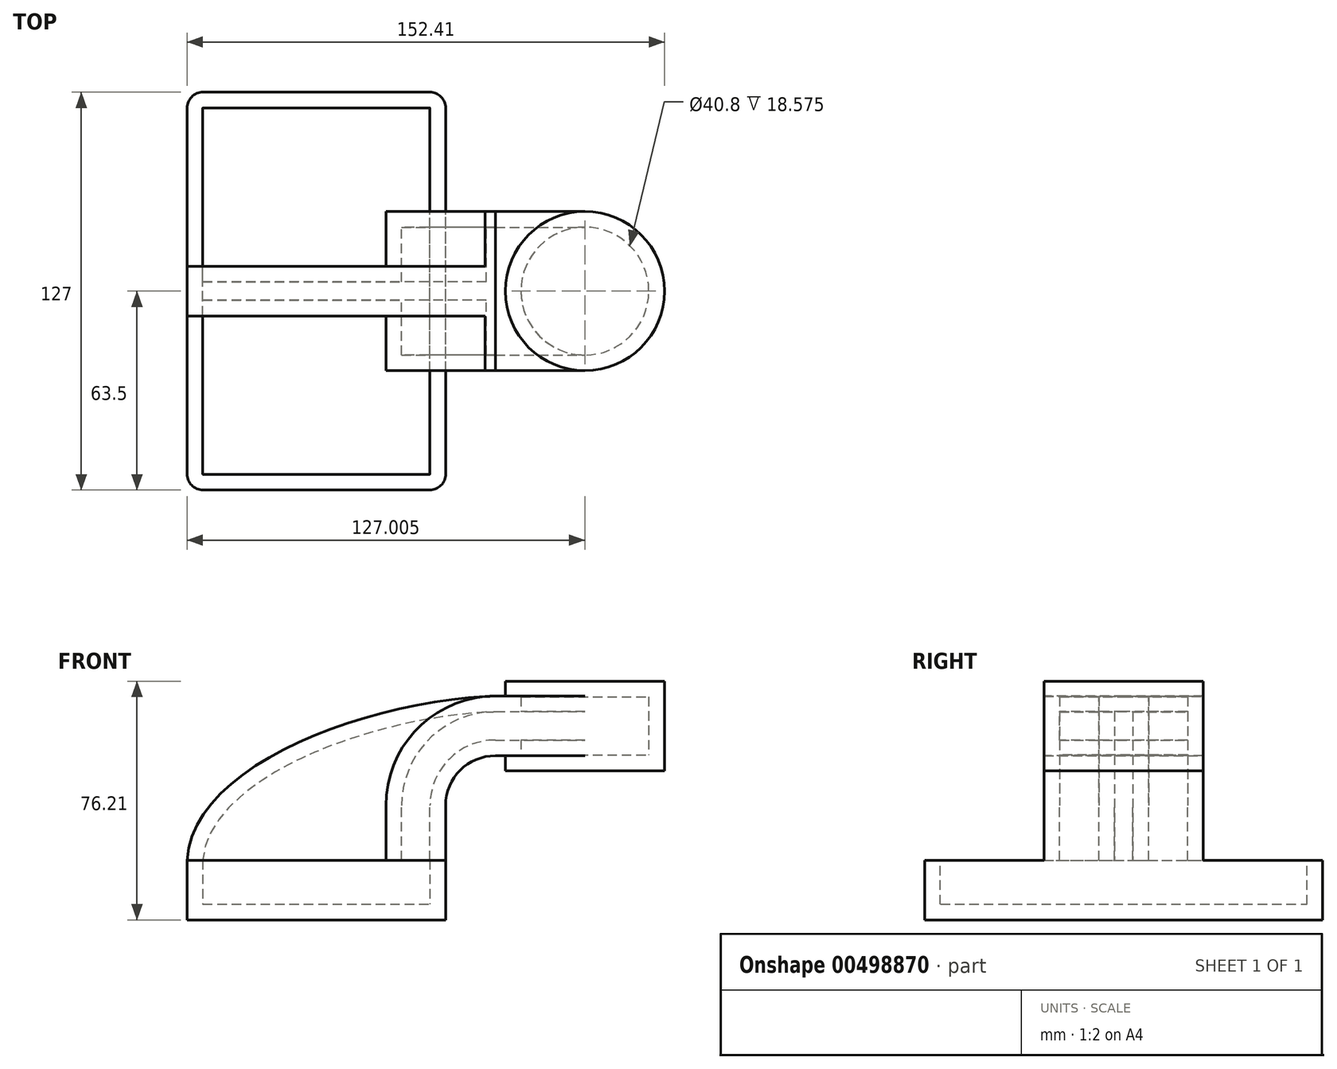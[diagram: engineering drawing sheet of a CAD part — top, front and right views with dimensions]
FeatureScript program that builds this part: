
annotation { "Feature Type Name" : "Feature", "Feature Type Description" : "" }
export const myFeature = defineFeature(function(context is Context, id is Id, definition is map)
    precondition{}
    {
        {
            var Q0;
            Q0=qCreatedBy(makeId("Front.planeOp"),FACE);
            var sketch = newSketch(context, id + "F0", { "sketchPlane" : qUnion([Q0])});
            skLineSegment(sketch, "E0.rect.bottom", {"start": v(-41.28, 9.52) * mm, "end": v(41.28, 9.52) * mm});
            skLineSegment(sketch, "E0.rect.top", {"start": v(-41.28, -9.52) * mm, "end": v(41.28, -9.52) * mm});
            skLineSegment(sketch, "E0.rect.left", {"start": v(-41.28, 9.52) * mm, "end": v(-41.28, -9.52) * mm});
            skLineSegment(sketch, "E0.rect.right", {"start": v(41.28, 9.52) * mm, "end": v(41.28, -9.52) * mm});
            skPoint(sketch, "E0.rect.middle", {"position": v(0, 0) * mm});
            skLineSegment(sketch, "E1", {"start": v(41.28, 9.52) * mm, "end": v(41.28, 27) * mm});
            skArc(sketch, "E2", {"start": v(41.28, 27) * mm, "mid": v(45.92, 38.23) * mm, "end": v(57.15, 42.88) * mm});
            skLineSegment(sketch, "E3", {"start": v(57.15, 42.88) * mm, "end": v(85.72, 42.88) * mm});
            skLineSegment(sketch, "E4.rect.bottom", {"start": v(60.32, 38.1) * mm, "end": v(111.12, 38.1) * mm});
            skLineSegment(sketch, "E4.rect.top", {"start": v(60.32, 66.68) * mm, "end": v(111.12, 66.68) * mm});
            skLineSegment(sketch, "E4.rect.left", {"start": v(60.32, 38.1) * mm, "end": v(60.32, 66.68) * mm});
            skLineSegment(sketch, "E4.rect.right", {"start": v(111.13, 38.1) * mm, "end": v(111.12, 66.68) * mm});
            skPoint(sketch, "E4.rect.middle", {"position": v(85.72, 52.39) * mm});
            skLineSegment(sketch, "E5.0", {"start": v(57.15, 61.93) * mm, "end": v(85.72, 61.93) * mm});
            skArc(sketch, "E5.1", {"start": v(22.23, 27) * mm, "mid": v(32.45, 51.7) * mm, "end": v(57.15, 61.93) * mm});
            skLineSegment(sketch, "E5.2", {"start": v(22.23, 9.52) * mm, "end": v(22.23, 27) * mm});
            skLineSegment(sketch, "E6", {"start": v(85.72, 38.1) * mm, "end": v(85.72, 66.68) * mm});
            skFitSpline(sketch, "E7", {"points": [v(-41.28, 9.53) * mm, v(57.15, 61.93) * mm], "startDerivative": vector(5.2, 92.34) * mm, "endDerivative": vector(120.92, 4.22) * mm});
            skSolve(sketch);
        }
        {
            var Q0;
            Q0=makeQuery(id+"F0.imprint","IMPRINT",FACE,{"disambiguationData":[TD([[makeQuery(id+"F0.imprint","IMPRINT",EDGE,{"derivedFrom":sQuery(id+"F0.wireOp",EDGE,"E0.rect.top")}),1.0]])]});
            extrude(context, id + "F1", {"entities" : qUnion([Q0]), "depth" : 127 * mm, "symmetric" : true});
        }
        {
            var Q0;
            {var subQ9=sQuery(id+"F0.wireOp",EDGE,"E1");Q0=makeQuery(id+"F0.imprint","IMPRINT",FACE,{"disambiguationData":[TD([[makeQuery(id+"F0.imprint","IMPRINT",EDGE,{"derivedFrom":subQ9}),1.0]])]});}
            var Q1;
            {var subQ0=sQuery(id+"F0.wireOp",EDGE,"E6");var subQ1=sQuery(id+"F0.wireOp",EDGE,"E3");var subQ2=makeQuery(id+"F0.imprint","INTERSECT",VERTEX,{"derivedFrom":[subQ1,subQ0]});Q1=makeQuery(id+"F0.imprint","IMPRINT",FACE,{"disambiguationData":[TD([[makeQuery(id+"F0.imprint","IMPRINT",EDGE,{"disambiguationData":[TD([[subQ2,1.0]])],"derivedFrom":subQ1}),1.0]])]});}
            extrude(context, id + "F2", {"entities" : qUnion([Q0, Q1]), "operationType" : NewBodyOperationType.ADD, "depth" : 50.8 * mm, "symmetric" : true});
        }
        {
            var Q0;
            {var subQ3=sQuery(id+"F0.wireOp",EDGE,"E5.2");Q0=makeQuery(id+"F0.imprint","IMPRINT",FACE,{"disambiguationData":[TD([[makeQuery(id+"F0.imprint","IMPRINT",EDGE,{"derivedFrom":subQ3}),1.0]])]});}
            extrude(context, id + "F3", {"entities" : qUnion([Q0]), "operationType" : NewBodyOperationType.ADD, "depth" : 15.88 * mm, "symmetric" : true});
        }
        {
            var Q0;
            {var subQ5=sQuery(id+"F0.wireOp",EDGE,"E4.rect.right");Q0=makeQuery(id+"F0.imprint","IMPRINT",FACE,{"disambiguationData":[TD([[makeQuery(id+"F0.imprint","IMPRINT",EDGE,{"derivedFrom":subQ5}),1.0]])]});}
            var Q1;
            Q1=sQuery(id+"F0.wireOp",EDGE,"E6");
            revolve(context, id + "F4", {"operationType" : NewBodyOperationType.ADD, "entities" : qUnion([Q0]), "axis" : qUnion([Q1]), "revolveType" : RevolveType.FULL});
        }
        {
            var Q0;
            Q0=makeQuery(id+"F1.opExtrude","CAP_EDGE",EDGE,{"disambiguationData":[OSD([sQuery(id+"F0.wireOp",EDGE,"E0.rect.right")])],"isStart":false});
            var Q1;
            Q1=makeQuery(id+"F1.opExtrude","CAP_EDGE",EDGE,{"disambiguationData":[OSD([sQuery(id+"F0.wireOp",EDGE,"E0.rect.left")])],"isStart":false});
            var Q2;
            Q2=makeQuery(id+"F1.opExtrude","CAP_EDGE",EDGE,{"disambiguationData":[OSD([sQuery(id+"F0.wireOp",EDGE,"E0.rect.right")])],"isStart":true});
            var Q3;
            Q3=makeQuery(id+"F1.opExtrude","CAP_EDGE",EDGE,{"disambiguationData":[OSD([sQuery(id+"F0.wireOp",EDGE,"E0.rect.left")])],"isStart":true});
            fillet(context, id + "F5", {"entities" : qUnion([Q0, Q1, Q2, Q3]), "radius" : 5.08 * mm, "tangentPropagation" : true, "allowEdgeOverflow" : false});
        }
        {
            var Q0;
            {var subQ4=sQuery(id+"F0.wireOp",EDGE,"E0.rect.bottom");var subQ5=sQuery(id+"F0.wireOp",EDGE,"E0.rect.right");var subQ6=sQuery(id+"F0.wireOp",EDGE,"E0.rect.left");Q0=makeQuery(id+"F3.boolean.opBoolean","SPLIT",FACE,{"disambiguationData":[TD([makeQuery(id+"F1.opExtrude","CAP_FACE",FACE,{"disambiguationData":[OSD([subQ4,sQuery(id+"F0.wireOp",EDGE,"E0.rect.top"),subQ6,subQ5])],"isStart":false})])],"derivedFrom":makeQuery(id+"F1.opExtrude","SWEPT_FACE",FACE,{"disambiguationData":[OSD([subQ4])]})});}
            var Q1;
            {var subQ4=sQuery(id+"F0.wireOp",EDGE,"E0.rect.bottom");var subQ5=sQuery(id+"F0.wireOp",EDGE,"E0.rect.right");var subQ6=sQuery(id+"F0.wireOp",EDGE,"E0.rect.left");Q1=makeQuery(id+"F3.boolean.opBoolean","SPLIT",FACE,{"disambiguationData":[TD([makeQuery(id+"F1.opExtrude","CAP_FACE",FACE,{"disambiguationData":[OSD([subQ4,sQuery(id+"F0.wireOp",EDGE,"E0.rect.top"),subQ6,subQ5])],"isStart":true})])],"derivedFrom":makeQuery(id+"F1.opExtrude","SWEPT_FACE",FACE,{"disambiguationData":[OSD([subQ4])]})});}
            shell(context, id + "F6", {"entities" : qUnion([Q0, Q1]), "thickness" : 5 * mm});
        }
    });
